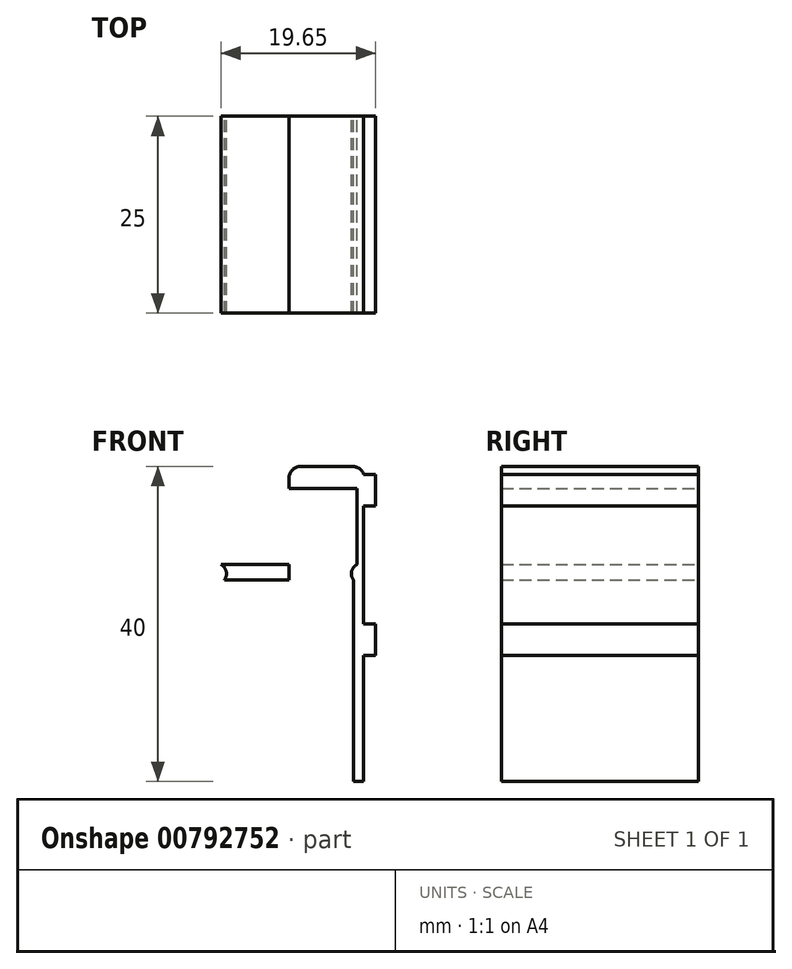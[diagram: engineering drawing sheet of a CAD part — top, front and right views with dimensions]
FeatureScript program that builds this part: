
annotation { "Feature Type Name" : "Feature", "Feature Type Description" : "" }
export const myFeature = defineFeature(function(context is Context, id is Id, definition is map)
    precondition{}
    {
        {
            var Q0;
            Q0=qCreatedBy(makeId("Front.planeOp"),FACE);
            var sketch = newSketch(context, id + "F0", { "sketchPlane" : qUnion([Q0])});
            skLineSegment(sketch, "E0", {"start": v(0, 20) * mm, "end": v(9.5, 20) * mm});
            skLineSegment(sketch, "E1", {"start": v(9.5, 20) * mm, "end": v(9.5, 19) * mm});
            skLineSegment(sketch, "E2", {"start": v(9.5, 19) * mm, "end": v(11, 19) * mm});
            skLineSegment(sketch, "E3", {"start": v(11, 19) * mm, "end": v(11, 15) * mm});
            skLineSegment(sketch, "E4", {"start": v(11, 15) * mm, "end": v(9.5, 15) * mm});
            skLineSegment(sketch, "E5", {"start": v(9.5, 15) * mm, "end": v(9.5, 0) * mm});
            skLineSegment(sketch, "E6", {"start": v(9.5, 0) * mm, "end": v(11, 0) * mm});
            skLineSegment(sketch, "E7", {"start": v(11, 0) * mm, "end": v(11, -4) * mm});
            skLineSegment(sketch, "E8", {"start": v(11, -4) * mm, "end": v(9.5, -4) * mm});
            skLineSegment(sketch, "E9", {"start": v(9.5, -4) * mm, "end": v(9.5, -20) * mm});
            skLineSegment(sketch, "E10", {"start": v(9.5, -20) * mm, "end": v(0, -20) * mm});
            skLineSegment(sketch, "E11", {"start": v(0, 20) * mm, "end": v(0, -20) * mm, "construction": true});
            skLineSegment(sketch, "E12", {"start": v(0, 20) * mm, "end": v(0, -20) * mm});
            skLineSegment(sketch, "E13", {"start": v(0, 17.18) * mm, "end": v(8.65, 17.18) * mm});
            skArc(sketch, "E14", {"start": v(8.65, 7.54) * mm, "mid": v(7.96, 6.67) * mm, "end": v(8.2, 5.58) * mm});
            skLineSegment(sketch, "E15", {"start": v(8.65, 7.54) * mm, "end": v(0, 7.54) * mm});
            skLineSegment(sketch, "E16", {"start": v(8.2, 5.58) * mm, "end": v(0, 5.58) * mm});
            skLineSegment(sketch, "E17", {"start": v(8.65, 7.54) * mm, "end": v(8.65, 17.18) * mm});
            skLineSegment(sketch, "E18", {"start": v(8.2, 5.58) * mm, "end": v(8.2, -20) * mm});
            skLineSegment(sketch, "E19.MirrorCS", {"start": v(-8.2, 5.58) * mm, "end": v(-8.2, -20) * mm});
            skLineSegment(sketch, "E20.MirrorCS", {"start": v(-8.2, 5.58) * mm, "end": v(0, 5.58) * mm});
            skArc(sketch, "E21.MirrorCS", {"start": v(-8.65, 7.54) * mm, "mid": v(-7.96, 6.67) * mm, "end": v(-8.2, 5.58) * mm});
            skLineSegment(sketch, "E22.MirrorCS", {"start": v(-8.65, 7.54) * mm, "end": v(0, 7.54) * mm});
            skLineSegment(sketch, "E23.MirrorCS", {"start": v(-8.65, 7.54) * mm, "end": v(-8.65, 17.18) * mm});
            skLineSegment(sketch, "E24.MirrorCS", {"start": v(-9.5, 15) * mm, "end": v(-9.5, 0) * mm});
            skLineSegment(sketch, "E25.MirrorCS", {"start": v(-9.5, 0) * mm, "end": v(-11, 0) * mm});
            skLineSegment(sketch, "E26.MirrorCS", {"start": v(-11, 0) * mm, "end": v(-11, -4) * mm});
            skLineSegment(sketch, "E27.MirrorCS", {"start": v(-9.5, -4) * mm, "end": v(-9.5, -20) * mm});
            skLineSegment(sketch, "E28.MirrorCS", {"start": v(-11, -4) * mm, "end": v(-9.5, -4) * mm});
            skLineSegment(sketch, "E29.MirrorCS", {"start": v(-11, 15) * mm, "end": v(-9.5, 15) * mm});
            skLineSegment(sketch, "E30.MirrorCS", {"start": v(0, 20) * mm, "end": v(-9.5, 20) * mm});
            skLineSegment(sketch, "E31.MirrorCS", {"start": v(-9.5, 20) * mm, "end": v(-9.5, 19) * mm});
            skLineSegment(sketch, "E32.MirrorCS", {"start": v(-11, 19) * mm, "end": v(-11, 15) * mm});
            skLineSegment(sketch, "E33.MirrorCS", {"start": v(-9.5, 19) * mm, "end": v(-11, 19) * mm});
            skLineSegment(sketch, "E34.MirrorCS", {"start": v(-9.5, -20) * mm, "end": v(0, -20) * mm});
            skLineSegment(sketch, "E35.MirrorCS", {"start": v(0, 17.18) * mm, "end": v(-8.65, 17.18) * mm});
            skLineSegment(sketch, "E36", {"start": v(-9.23, 6.38) * mm, "end": v(9.23, 6.38) * mm, "construction": true});
            skSolve(sketch);
        }
        {
            var Q0;
            {var subQ1=sQuery(id+"F0.wireOp",EDGE,"E0");Q0=makeQuery(id+"F0.imprint","IMPRINT",FACE,{"disambiguationData":[TD([[makeQuery(id+"F0.imprint","IMPRINT",EDGE,{"derivedFrom":subQ1}),-1.0]])]});}
            var Q1;
            Q1=makeQuery(id+"F0.imprint","IMPRINT",FACE,{"disambiguationData":[TD([[makeQuery(id+"F0.imprint","IMPRINT",EDGE,{"derivedFrom":sQuery(id+"F0.wireOp",EDGE,"E21.MirrorCS")}),-1.0]])]});
            extrude(context, id + "F1", {"entities" : qUnion([Q0, Q1]), "depth" : 25 * mm, "offsetDistance" : 25 * mm});
        }
        {
            var Q0;
            Q0=makeQuery(id+"F1.opExtrude","SWEPT_EDGE",EDGE,{"disambiguationData":[OSD([sQuery(id+"F0.wireOp",EDGE,"E30.MirrorCS"),sQuery(id+"F0.wireOp",EDGE,"E31.MirrorCS")])]});
            var Q1;
            Q1=makeQuery(id+"F1.opExtrude","SWEPT_EDGE",EDGE,{"disambiguationData":[OSD([sQuery(id+"F0.wireOp",EDGE,"E0"),sQuery(id+"F0.wireOp",EDGE,"E1")])]});
            fillet(context, id + "F2", {"entities" : qUnion([Q0, Q1]), "radius" : 1.5 * mm, "tangentPropagation" : true, "allowEdgeOverflow" : false});
        }
    });
